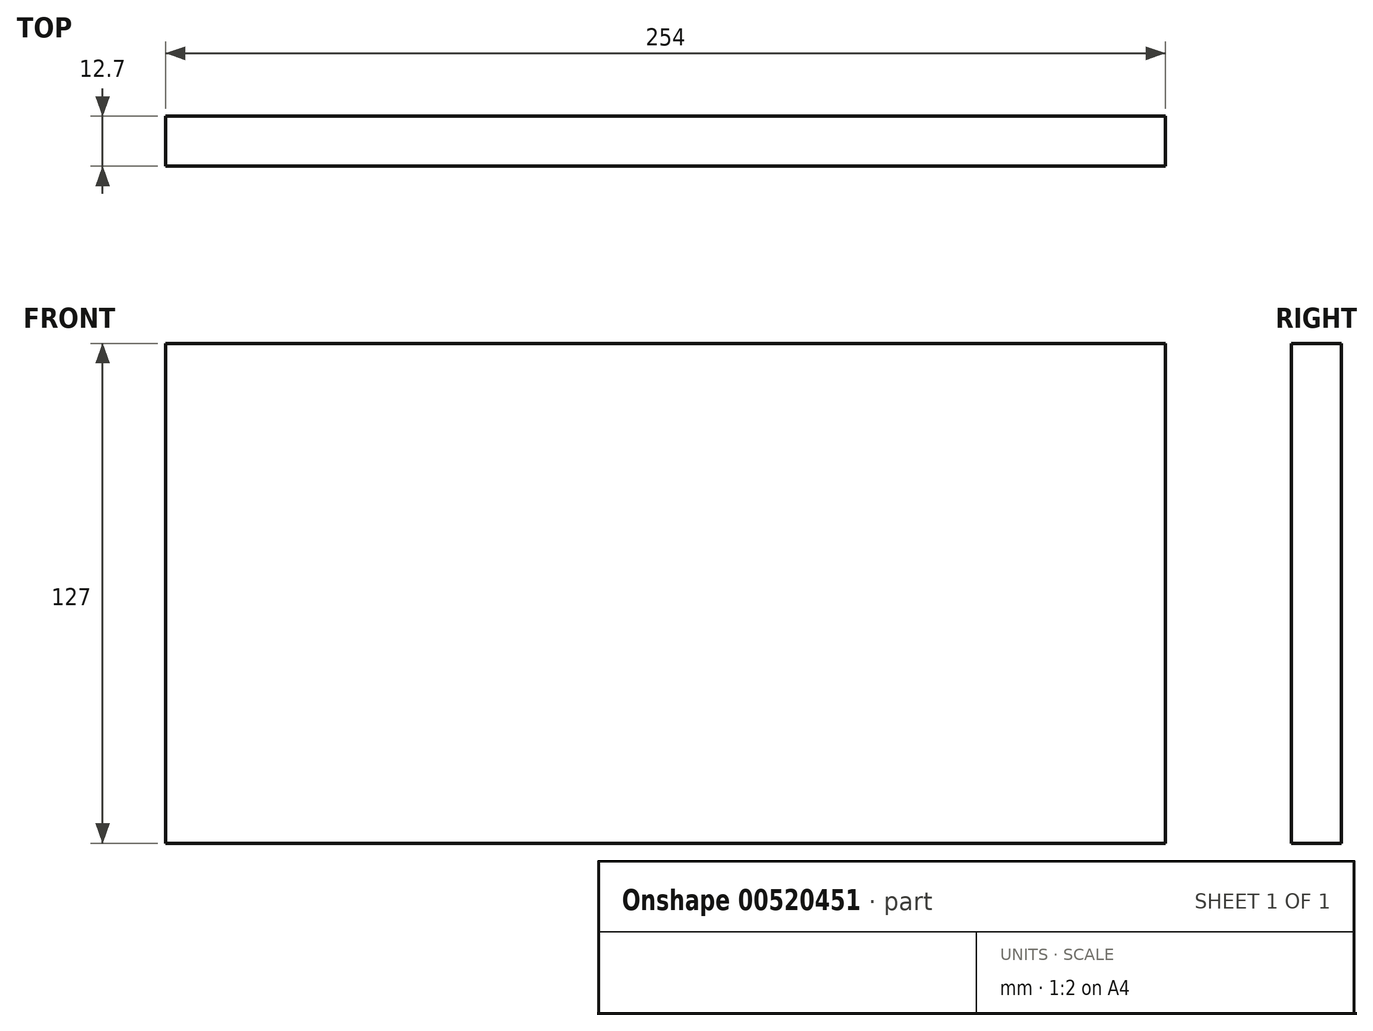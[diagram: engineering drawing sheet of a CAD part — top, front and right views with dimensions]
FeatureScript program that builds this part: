
annotation { "Feature Type Name" : "Feature", "Feature Type Description" : "" }
export const myFeature = defineFeature(function(context is Context, id is Id, definition is map)
    precondition{}
    {
        {
            var Q0;
            Q0=qCreatedBy(makeId("Front.planeOp"),FACE);
            var sketch = newSketch(context, id + "F0", { "sketchPlane" : qUnion([Q0])});
            skLineSegment(sketch, "E0.bottom", {"start": v(-110.5, 61.37) * mm, "end": v(143.5, 61.37) * mm});
            skLineSegment(sketch, "E0.top", {"start": v(-110.5, -65.63) * mm, "end": v(143.5, -65.63) * mm});
            skLineSegment(sketch, "E0.left", {"start": v(-110.5, 61.37) * mm, "end": v(-110.5, -65.63) * mm});
            skLineSegment(sketch, "E0.right", {"start": v(143.5, 61.37) * mm, "end": v(143.5, -65.63) * mm});
            skSolve(sketch);
        }
        {
            var Q0;
            Q0=makeQuery(id+"F0.imprint","IMPRINT",FACE,{"disambiguationData":[TD([[makeQuery(id+"F0.imprint","IMPRINT",EDGE,{"derivedFrom":sQuery(id+"F0.wireOp",EDGE,"E0.bottom")}),-1.0]])]});
            extrude(context, id + "F1", {"entities" : qUnion([Q0]), "depth" : 12.7 * mm, "offsetDistance" : 25.4 * mm});
        }
    });
